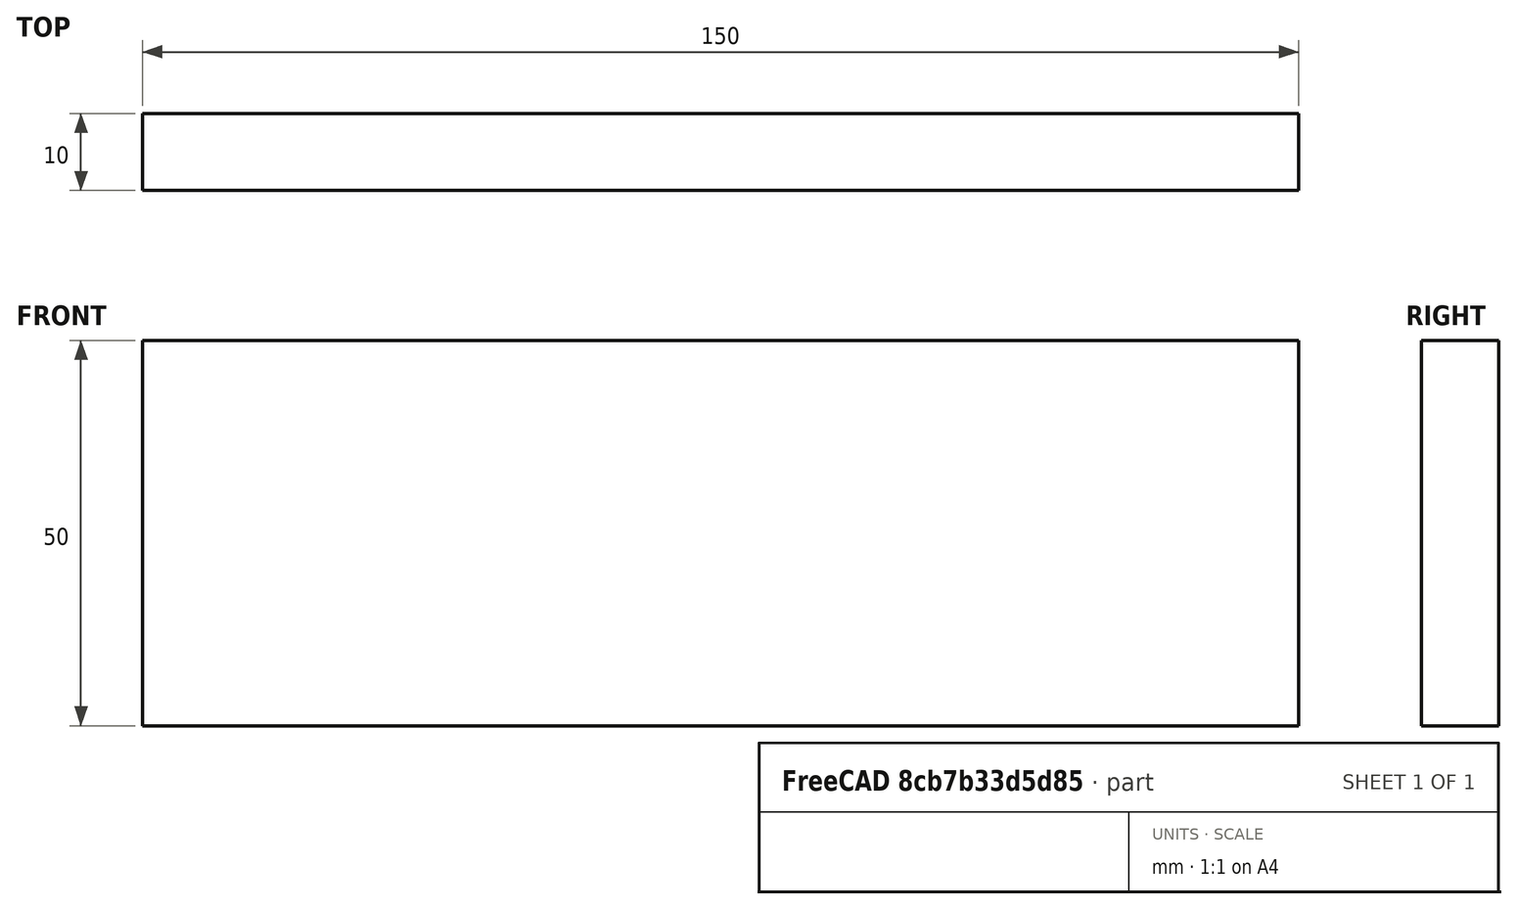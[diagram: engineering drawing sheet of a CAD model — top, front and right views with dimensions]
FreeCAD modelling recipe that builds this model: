
FCSTD DOCUMENT  (FreeCAD 0.15R4671 (Git))
Label: Flat Bar 150x10 EN10058 S235JR
License: All rights reserved
LicenseURL: http://en.wikipedia.org/wiki/All_rights_reserved
objects: Sketcher::SketchObject×1, Part::Extrusion×1
note: 2 computed .brp shape members not serialized (recipe doc carries the construction recipe); baked Part::Feature solids carry a one-line shape summary decoded from their .brp

FEATURE [Sketcher::SketchObject] Sketch
  sketch-geometry (4):
    g0: LineSegment StartX=-75 StartY=-5 StartZ=0 EndX=75 EndY=-5 EndZ=0
    g1: LineSegment StartX=75 StartY=-5 StartZ=0 EndX=75 EndY=5 EndZ=0
    g2: LineSegment StartX=75 StartY=5 StartZ=0 EndX=-75 EndY=5 EndZ=0
    g3: LineSegment StartX=-75 StartY=5 StartZ=0 EndX=-75 EndY=-5 EndZ=0
  constraints (12):
    c: Coincident(g0,g1)
    c: Coincident(g1,g2)
    c: Coincident(g2,g3)
    c: Coincident(g3,g0)
    c: Horizontal(g0)
    c: Horizontal(g2)
    c: Vertical(g1)
    c: Vertical(g3)
    c: Symmetric(g1,g2,g-2)
    c: Symmetric(g0,g1,g-1)
    c: DistanceY(g1) = 10
    c: DistanceX(g0) = 150
FEATURE [Part::Extrusion] Extrude  label="Flat Bar 150x10 EN10058 S235JR"
  Base = -> Sketch
  Dir = (0,0,50)
  Solid = true
